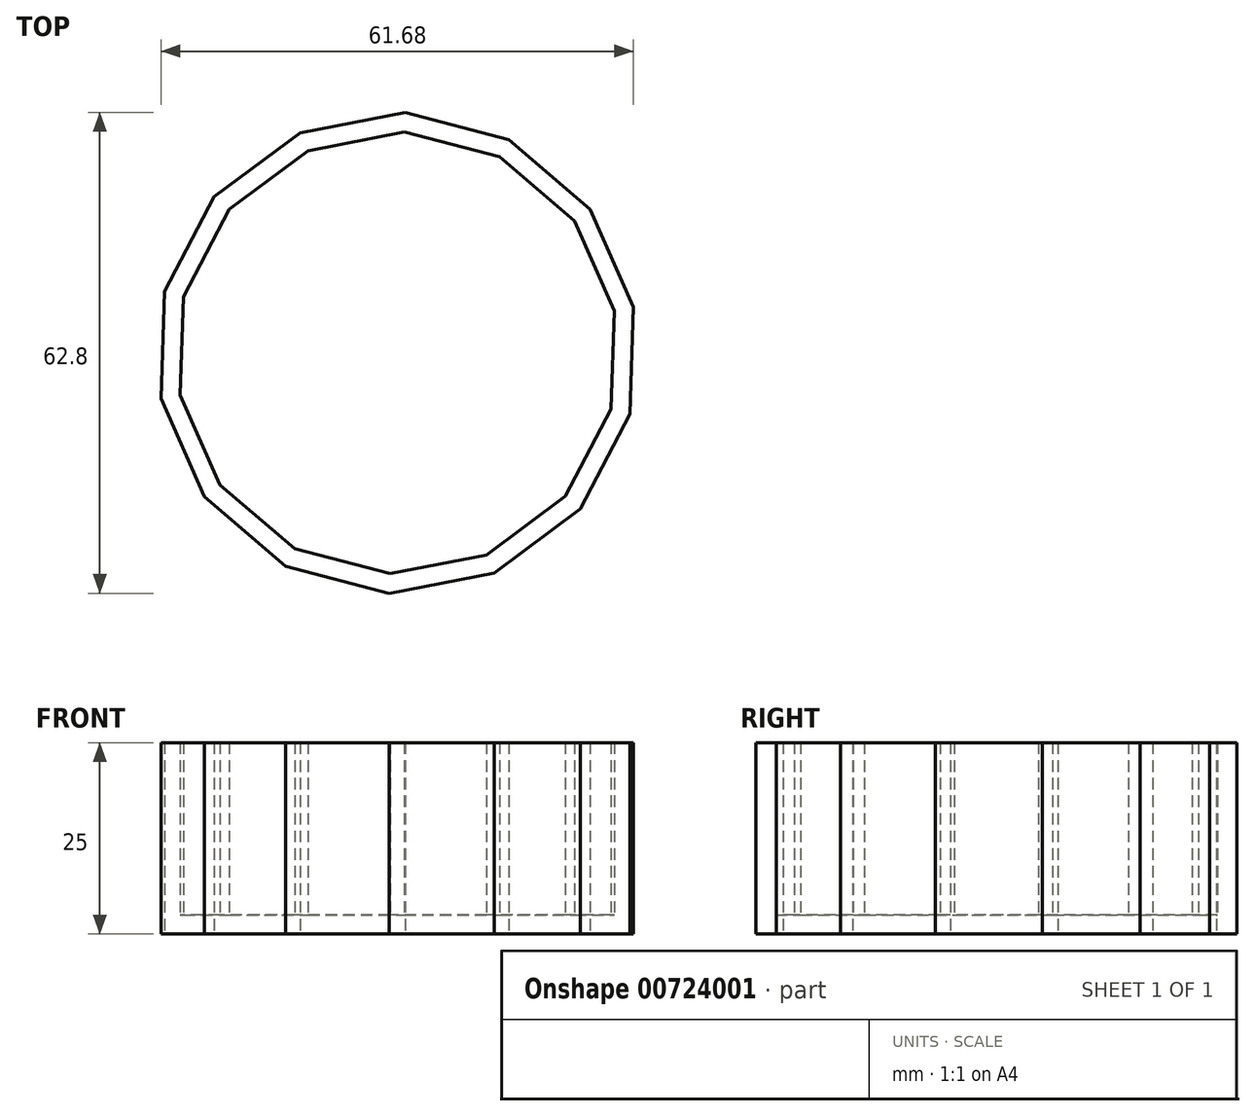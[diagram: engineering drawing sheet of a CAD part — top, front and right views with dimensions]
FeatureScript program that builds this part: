
annotation { "Feature Type Name" : "Feature", "Feature Type Description" : "" }
export const myFeature = defineFeature(function(context is Context, id is Id, definition is map)
    precondition{}
    {
        {
            var Q0;
            Q0=qCreatedBy(makeId("Top.planeOp"),FACE);
            var sketch = newSketch(context, id + "F0", { "sketchPlane" : qUnion([Q0])});
            skCircle(sketch, "E0.cCircle", {"center": v(0, 0) * mm, "radius": 30.63 * mm, "construction": true});
            skLineSegment(sketch, "E0.0", {"start": v(-23.9, 20.38) * mm, "end": v(-12.7, 28.74) * mm});
            skLineSegment(sketch, "E0.1", {"start": v(-12.7, 28.74) * mm, "end": v(1.03, 31.4) * mm});
            skLineSegment(sketch, "E0.2", {"start": v(1.03, 31.4) * mm, "end": v(14.55, 27.84) * mm});
            skLineSegment(sketch, "E0.3", {"start": v(14.55, 27.84) * mm, "end": v(25.2, 18.77) * mm});
            skLineSegment(sketch, "E0.4", {"start": v(25.2, 18.77) * mm, "end": v(30.84, 5.98) * mm});
            skLineSegment(sketch, "E0.5", {"start": v(30.84, 5.98) * mm, "end": v(30.38, -8) * mm});
            skLineSegment(sketch, "E0.6", {"start": v(30.38, -8) * mm, "end": v(23.9, -20.38) * mm});
            skLineSegment(sketch, "E0.7", {"start": v(23.9, -20.38) * mm, "end": v(12.7, -28.74) * mm});
            skLineSegment(sketch, "E0.8", {"start": v(12.7, -28.74) * mm, "end": v(-1.03, -31.4) * mm});
            skLineSegment(sketch, "E0.9", {"start": v(-1.03, -31.4) * mm, "end": v(-14.55, -27.84) * mm});
            skLineSegment(sketch, "E0.10", {"start": v(-14.55, -27.84) * mm, "end": v(-25.2, -18.77) * mm});
            skLineSegment(sketch, "E0.11", {"start": v(-25.2, -18.77) * mm, "end": v(-30.84, -5.98) * mm});
            skLineSegment(sketch, "E0.12", {"start": v(-30.84, -5.98) * mm, "end": v(-30.38, 8) * mm});
            skLineSegment(sketch, "E0.13", {"start": v(-30.38, 8) * mm, "end": v(-23.9, 20.38) * mm});
            skPoint(sketch, "E0.0.midPoint", {"position": v(-18.3, 24.56) * mm});
            skSolve(sketch);
        }
        {
            var Q0;
            Q0=makeQuery(id+"F0.imprint","IMPRINT",FACE,{"disambiguationData":[TD([[makeQuery(id+"F0.imprint","IMPRINT",EDGE,{"derivedFrom":sQuery(id+"F0.wireOp",EDGE,"E0.0")}),-1.0]])]});
            extrude(context, id + "F1", {"entities" : qUnion([Q0]), "depth" : 25 * mm, "offsetDistance" : 25 * mm});
        }
        {
            var Q0;
            Q0=makeQuery(id+"F1.opExtrude","CAP_FACE",FACE,{"disambiguationData":[OSD([sQuery(id+"F0.wireOp",EDGE,"E0.0"),sQuery(id+"F0.wireOp",EDGE,"E0.1"),sQuery(id+"F0.wireOp",EDGE,"E0.2"),sQuery(id+"F0.wireOp",EDGE,"E0.3"),sQuery(id+"F0.wireOp",EDGE,"E0.4"),sQuery(id+"F0.wireOp",EDGE,"E0.5"),sQuery(id+"F0.wireOp",EDGE,"E0.6"),sQuery(id+"F0.wireOp",EDGE,"E0.7"),sQuery(id+"F0.wireOp",EDGE,"E0.8"),sQuery(id+"F0.wireOp",EDGE,"E0.9"),sQuery(id+"F0.wireOp",EDGE,"E0.10"),sQuery(id+"F0.wireOp",EDGE,"E0.11"),sQuery(id+"F0.wireOp",EDGE,"E0.12"),sQuery(id+"F0.wireOp",EDGE,"E0.13")])],"isStart":false});
            shell(context, id + "F2", {"entities" : qUnion([Q0]), "thickness" : 2.5 * mm});
        }
    });
